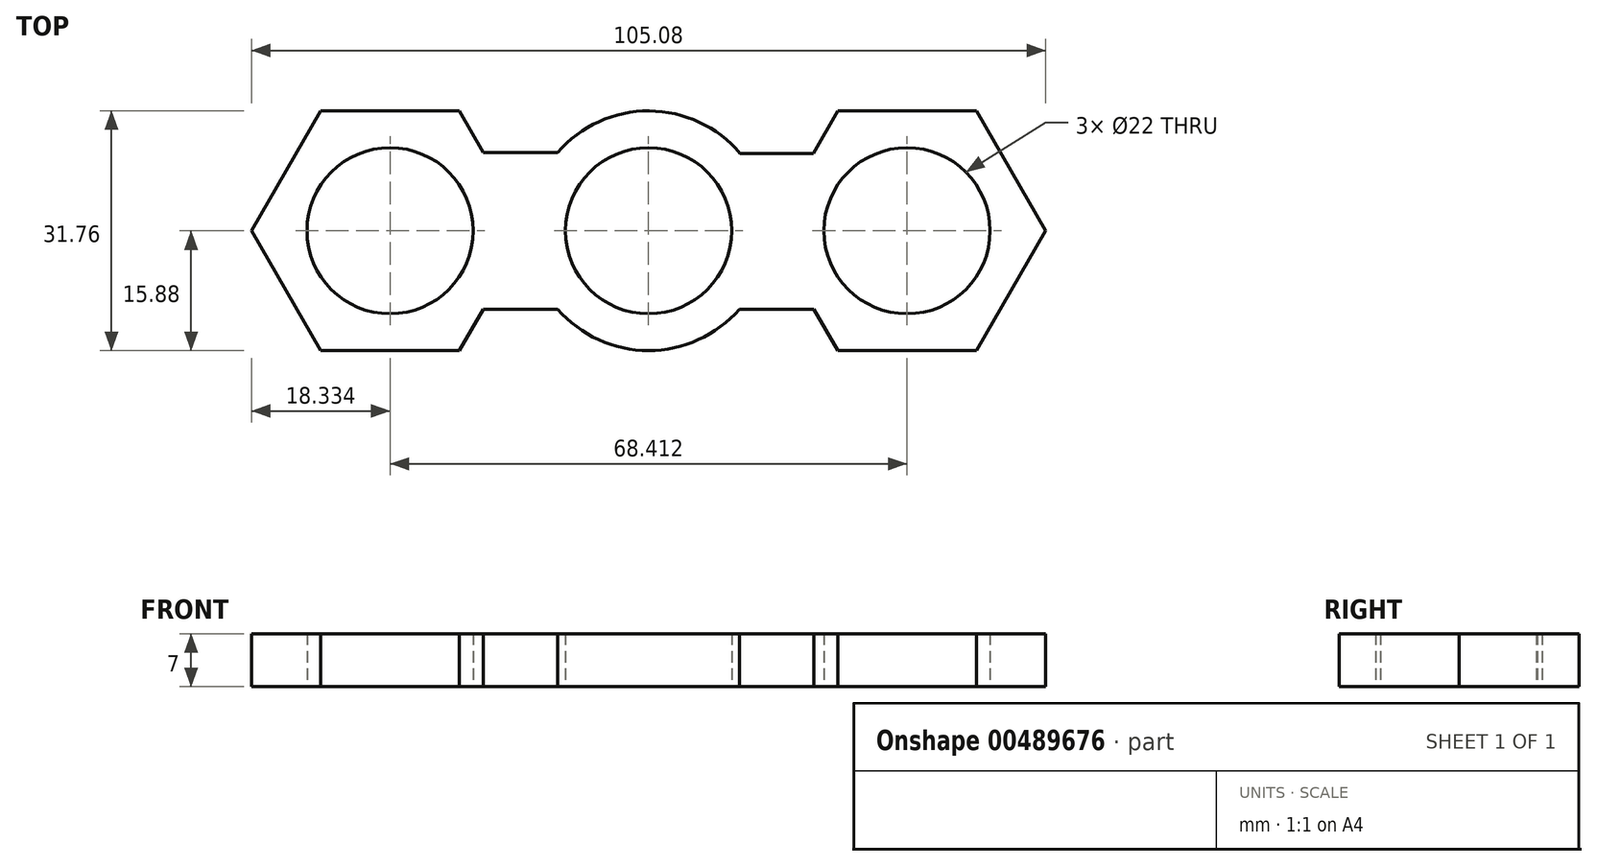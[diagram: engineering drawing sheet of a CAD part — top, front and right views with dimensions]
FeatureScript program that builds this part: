
annotation { "Feature Type Name" : "Feature", "Feature Type Description" : "" }
export const myFeature = defineFeature(function(context is Context, id is Id, definition is map)
    precondition{}
    {
        {
            var Q0;
            Q0=qCreatedBy(makeId("Top.planeOp"),FACE);
            var sketch = newSketch(context, id + "F0", { "sketchPlane" : qUnion([Q0])});
            skCircle(sketch, "E0.cCircle", {"center": v(-34.2, 0) * mm, "radius": 15.88 * mm, "construction": true});
            skLineSegment(sketch, "E0.0", {"start": v(-15.88, 0) * mm, "end": v(-25.04, -15.87) * mm});
            skLineSegment(sketch, "E0.1", {"start": v(-25.04, -15.87) * mm, "end": v(-43.37, -15.87) * mm});
            skLineSegment(sketch, "E0.2", {"start": v(-43.37, -15.88) * mm, "end": v(-52.54, 0) * mm});
            skLineSegment(sketch, "E0.3", {"start": v(-52.54, 0) * mm, "end": v(-43.37, 15.87) * mm});
            skLineSegment(sketch, "E0.4", {"start": v(-43.37, 15.87) * mm, "end": v(-25.04, 15.87) * mm});
            skLineSegment(sketch, "E0.5", {"start": v(-25.04, 15.87) * mm, "end": v(-15.88, 0) * mm});
            skCircle(sketch, "E1.cCircle", {"center": v(34.2, 0) * mm, "radius": 15.88 * mm, "construction": true});
            skLineSegment(sketch, "E1.0", {"start": v(52.54, 0) * mm, "end": v(43.37, -15.88) * mm});
            skLineSegment(sketch, "E1.1", {"start": v(43.37, -15.87) * mm, "end": v(25.04, -15.88) * mm});
            skLineSegment(sketch, "E1.2", {"start": v(25.04, -15.88) * mm, "end": v(15.88, 0) * mm});
            skLineSegment(sketch, "E1.3", {"start": v(15.88, 0) * mm, "end": v(25.04, 15.87) * mm});
            skLineSegment(sketch, "E1.4", {"start": v(25.04, 15.87) * mm, "end": v(43.37, 15.88) * mm});
            skLineSegment(sketch, "E1.5", {"start": v(43.37, 15.87) * mm, "end": v(52.54, 0) * mm});
            skPoint(sketch, "E1.0.midPoint", {"position": v(47.95, -7.94) * mm});
            skCircle(sketch, "E2", {"center": v(0, 0) * mm, "radius": 15.88 * mm});
            skCircle(sketch, "E3", {"center": v(0, 0) * mm, "radius": 11 * mm});
            skPoint(sketch, "E4.startSnap0", {"position": v(-20.46, -7.94) * mm});
            skLineSegment(sketch, "E5", {"start": v(-21.87, -10.38) * mm, "end": v(-12.01, -10.38) * mm});
            skLineSegment(sketch, "E6", {"start": v(-21.87, 10.38) * mm, "end": v(-12.01, 10.38) * mm});
            skLineSegment(sketch, "E7", {"start": v(22.09, 10.25) * mm, "end": v(12.12, 10.25) * mm});
            skLineSegment(sketch, "E8", {"start": v(21.87, -10.38) * mm, "end": v(12.01, -10.38) * mm});
            skCircle(sketch, "E9", {"center": v(-34.2, 0) * mm, "radius": 11 * mm});
            skCircle(sketch, "E10", {"center": v(34.2, 0) * mm, "radius": 11 * mm});
            skSolve(sketch);
        }
        {
            var Q0;
            {var subQ0=sQuery(id+"F0.wireOp",EDGE,"E0.1");Q0=makeQuery(id+"F0.imprint","IMPRINT",FACE,{"disambiguationData":[TD([[makeQuery(id+"F0.imprint","IMPRINT",EDGE,{"derivedFrom":subQ0}),-1.0]])]});}
            var Q1;
            Q1=makeQuery(id+"F0.imprint","IMPRINT",FACE,{"disambiguationData":[TD([[makeQuery(id+"F0.imprint","IMPRINT",EDGE,{"derivedFrom":sQuery(id+"F0.wireOp",EDGE,"E3")}),-1.0]])]});
            var Q2;
            {var subQ3=sQuery(id+"F0.wireOp",EDGE,"E6");Q2=makeQuery(id+"F0.imprint","IMPRINT",FACE,{"disambiguationData":[TD([[makeQuery(id+"F0.imprint","IMPRINT",EDGE,{"derivedFrom":subQ3}),-1.0]])]});}
            var Q3;
            {var subQ3=sQuery(id+"F0.wireOp",EDGE,"E5");Q3=makeQuery(id+"F0.imprint","IMPRINT",FACE,{"disambiguationData":[TD([[makeQuery(id+"F0.imprint","IMPRINT",EDGE,{"derivedFrom":subQ3}),1.0]])]});}
            var Q4;
            {var subQ3=sQuery(id+"F0.wireOp",EDGE,"E8");Q4=makeQuery(id+"F0.imprint","IMPRINT",FACE,{"disambiguationData":[TD([[makeQuery(id+"F0.imprint","IMPRINT",EDGE,{"derivedFrom":subQ3}),-1.0]])]});}
            var Q5;
            {var subQ0=sQuery(id+"F0.wireOp",EDGE,"E2");var subQ3=sQuery(id+"F0.wireOp",EDGE,"E7");var subQ5=makeQuery(id+"F0.imprint","INTERSECT",VERTEX,{"derivedFrom":[subQ0,subQ3]});Q5=makeQuery(id+"F0.imprint","IMPRINT",FACE,{"disambiguationData":[TD([[makeQuery(id+"F0.imprint","IMPRINT",EDGE,{"disambiguationData":[TD([[subQ5,1.0]])],"derivedFrom":subQ3}),1.0]])]});}
            var Q6;
            Q6=makeQuery(id+"F0.imprint","IMPRINT",FACE,{"disambiguationData":[TD([[makeQuery(id+"F0.imprint","IMPRINT",EDGE,{"derivedFrom":sQuery(id+"F0.wireOp",EDGE,"E1.0")}),-1.0]])]});
            extrude(context, id + "F1", {"entities" : qUnion([Q0, Q1, Q2, Q3, Q4, Q5, Q6]), "depth" : 7 * mm, "offsetDistance" : 25.4 * mm});
        }
    });
